# Revit family: okamura_C783BR-C784BR-C783BS-C784BS_Finora_Middle Back Cushion Seat Adjustable Arm 1
name_source: partatom
category: Furniture
revit_build: Autodesk Revit 2017 (Build: 20160225_1515(x64)
units: mm (PartAtom-declared; Revit-internal decimal feet)

## family parameters
Always vertical = Yes
Cut with Voids When Loaded = No
OmniClass Number = 23.40.20.00
OmniClass Title = General Furniture and Specialties
Room Calculation Point = No
Shared = No
Work Plane-Based = No

## types (4) — shared parameters
Arm pad = okm_grey
Assembly Code = E2020200
Base = okm_grey
Body = okm_grey
Casters = okm_grey
Cushion Seat = okm_grey
Custom panel = okm_grey
D = 590 mm  [stored 1.9357 ft]
Gas lift = okm_grey
H = 1041 mm
Keynote = 12490
Kind = Chair
Manufacturer = Okamura Corporation
Mesh Back = okm_grey mesh
Product Categories = Seating
W = 690 mm  [stored 2.26378 ft]

## per-type parameters (varying)
| type | Common Specification | Hanger | Lumbar | Product Number | URL |
| C784BR_Option - Hanger | Option - Hanger | Yes | No | C784BR | http://www.okamura.co.jp |
| C783BR |  | No | No | C783BR | http://www.okamura.com |
| C783BS_Option - Lumbar | Option - Lumbar | No | Yes | C783BS | http://www.okamura.co.jp |
| C784BS_Option - Hanger&Lumbar | Option - Hanger&Lumbar | Yes | Yes | C784BS | http://www.okamura.co.jp |

note: [stored X ft] marks values corroborated as IEEE doubles in the binary element streams (Revit-internal decimal feet)
